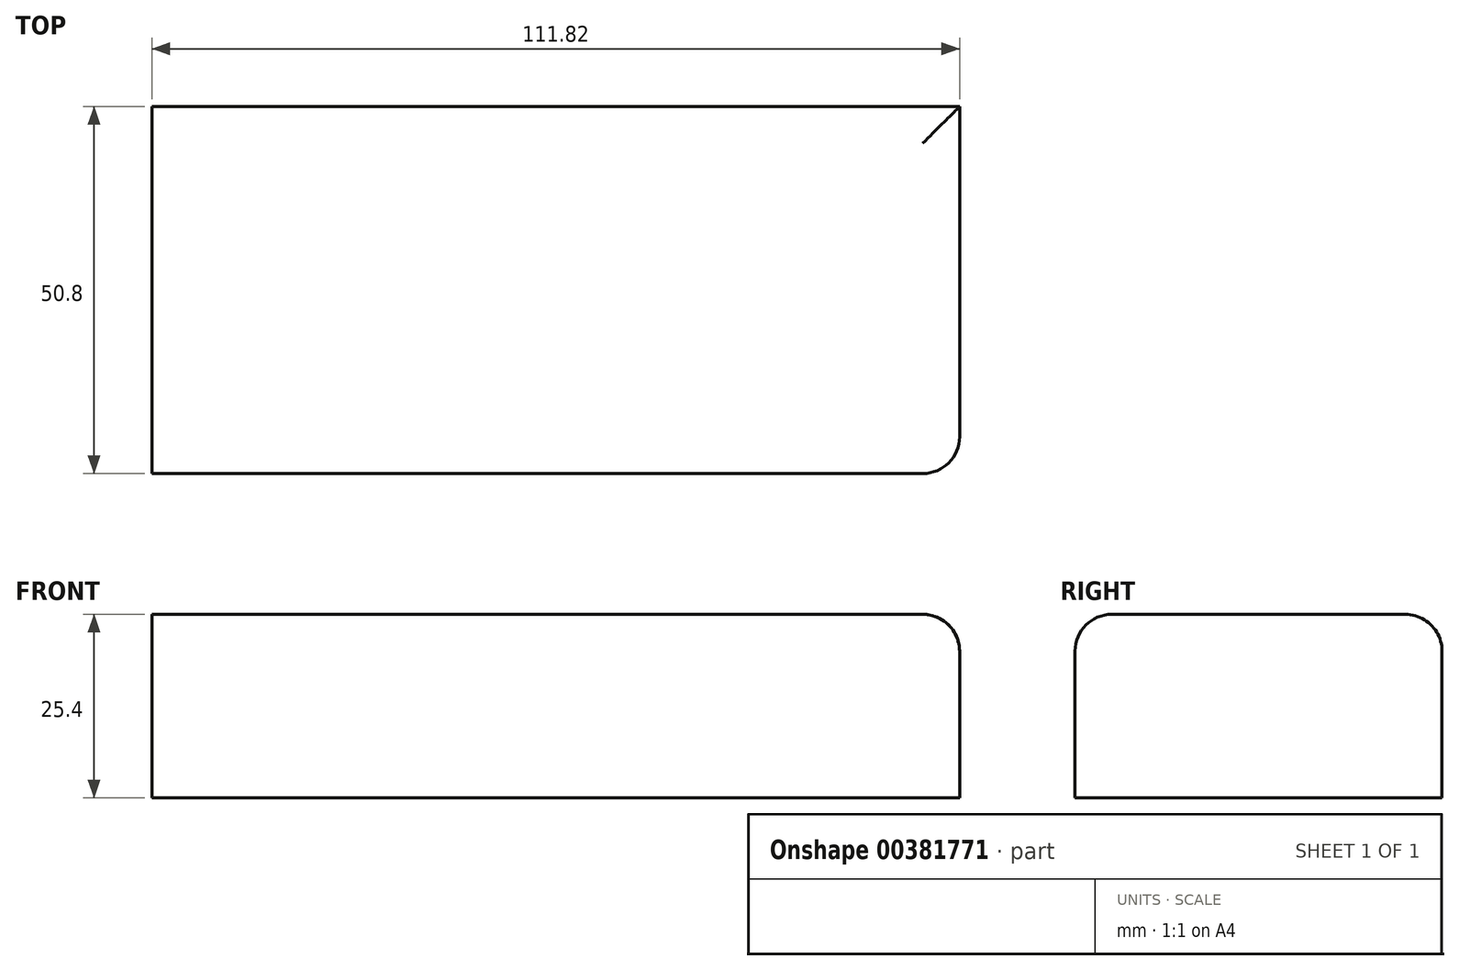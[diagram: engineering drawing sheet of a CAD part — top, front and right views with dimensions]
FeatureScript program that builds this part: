
annotation { "Feature Type Name" : "Feature", "Feature Type Description" : "" }
export const myFeature = defineFeature(function(context is Context, id is Id, definition is map)
    precondition{}
    {
        {
            var Q0;
            Q0=qCreatedBy(makeId("Top.planeOp"),FACE);
            var sketch = newSketch(context, id + "F0", { "sketchPlane" : qUnion([Q0])});
            skLineSegment(sketch, "E0.bottom", {"start": v(0, 25.4) * mm, "end": v(111.82, 25.4) * mm});
            skLineSegment(sketch, "E0.top", {"start": v(0, -25.4) * mm, "end": v(111.82, -25.4) * mm});
            skLineSegment(sketch, "E0.left", {"start": v(0, 25.4) * mm, "end": v(0, -25.4) * mm});
            skLineSegment(sketch, "E0.right", {"start": v(111.82, 25.4) * mm, "end": v(111.82, -25.4) * mm});
            skLineSegment(sketch, "E1", {"start": v(0, 0) * mm, "end": v(111.82, 0) * mm, "construction": true});
            skPoint(sketch, "E1.endSnap0", {"position": v(111.82, 0) * mm});
            skSolve(sketch);
        }
        {
            var Q0;
            Q0 = qSketchRegion(id + "F0", true);
            extrude(context, id + "F1", {"entities" : qUnion([Q0]), "depth" : 25.4 * mm});
        }
        {
            var Q0;
            Q0=makeQuery(id+"F1.opExtrude","CAP_EDGE",EDGE,{"disambiguationData":[OSD([sQuery(id+"F0.wireOp",EDGE,"E0.top")])],"isStart":false});
            var Q1;
            Q1=makeQuery(id+"F1.opExtrude","SWEPT_EDGE",EDGE,{"disambiguationData":[OSD([sQuery(id+"F0.wireOp",EDGE,"E0.top"),sQuery(id+"F0.wireOp",EDGE,"E0.right")])]});
            var Q2;
            Q2=makeQuery(id+"F1.opExtrude","CAP_EDGE",EDGE,{"disambiguationData":[OSD([sQuery(id+"F0.wireOp",EDGE,"E0.right")])],"isStart":false});
            var Q3;
            Q3=makeQuery(id+"F1.opExtrude","CAP_EDGE",EDGE,{"disambiguationData":[OSD([sQuery(id+"F0.wireOp",EDGE,"E0.bottom")])],"isStart":false});
            fillet(context, id + "F2", {"entities" : qUnion([Q0, Q1, Q2, Q3]), "radius" : 5.08 * mm, "tangentPropagation" : true, "allowEdgeOverflow" : false});
        }
    });
